# Revit family: HL_RU_Plug-in drain Primus_HL73Pr-A-171212
name_source: partatom
category: Instalační zařizovací předměty
units: mm (PartAtom-declared; Revit-internal decimal feet)

## family parameters
Bod výpočtu místnosti = Ano
Kóta kulaté spojky = Použít průměr
Nadpis OmniClass = Deck Waste Water Drains
Ořezat dutým tvarem při načtení = Ne
Sdílené = Ne
Typ dílu = Normální
Vždy vertikální = Ano
Založené na pracovní rovině = Ne
Číslo OmniClass = 23.70.50.21.24.14

## types (1)
- HL_Универсальный трап вертикальный_HL73Pr
    Cena = 0 $
    EAN = 9003076032327
    Indexovaná poznámka = HL73Pr
    Komentáře k typům = Универсальный трап вертикальный DN110 
с "сухим" сифоном
    Model = HL73Pr
    Popis = Трап для внутренних помещений
    URL = http://www.hutterer-lechner.com
    Výchozí výška = 0 mm  [stored 0 ft]
    Výrobce = HL Hutterer & Lechner GmbH
    ВЕС = 0,457 kg
    МАКСИМАЛЬНАЯ НАГРУЗКА КЛАССА = K3 - 300 kg
    МАТЕРИАЛ = PP / Edelstahl V2A
    НАСАДКА = 121x121mm
    НОМИНАЛЬНЫЙ ДИАМЕТР = 110 mm
    ПРОИЗВОДИТЕЛЬНОСТЬ = 0,46 l/s
    РАЗМЕР = DN110
    РЕШЁТКА = 115x115mm/ V2A

note: [stored X ft] marks values corroborated as IEEE doubles in the binary element streams (Revit-internal decimal feet)
